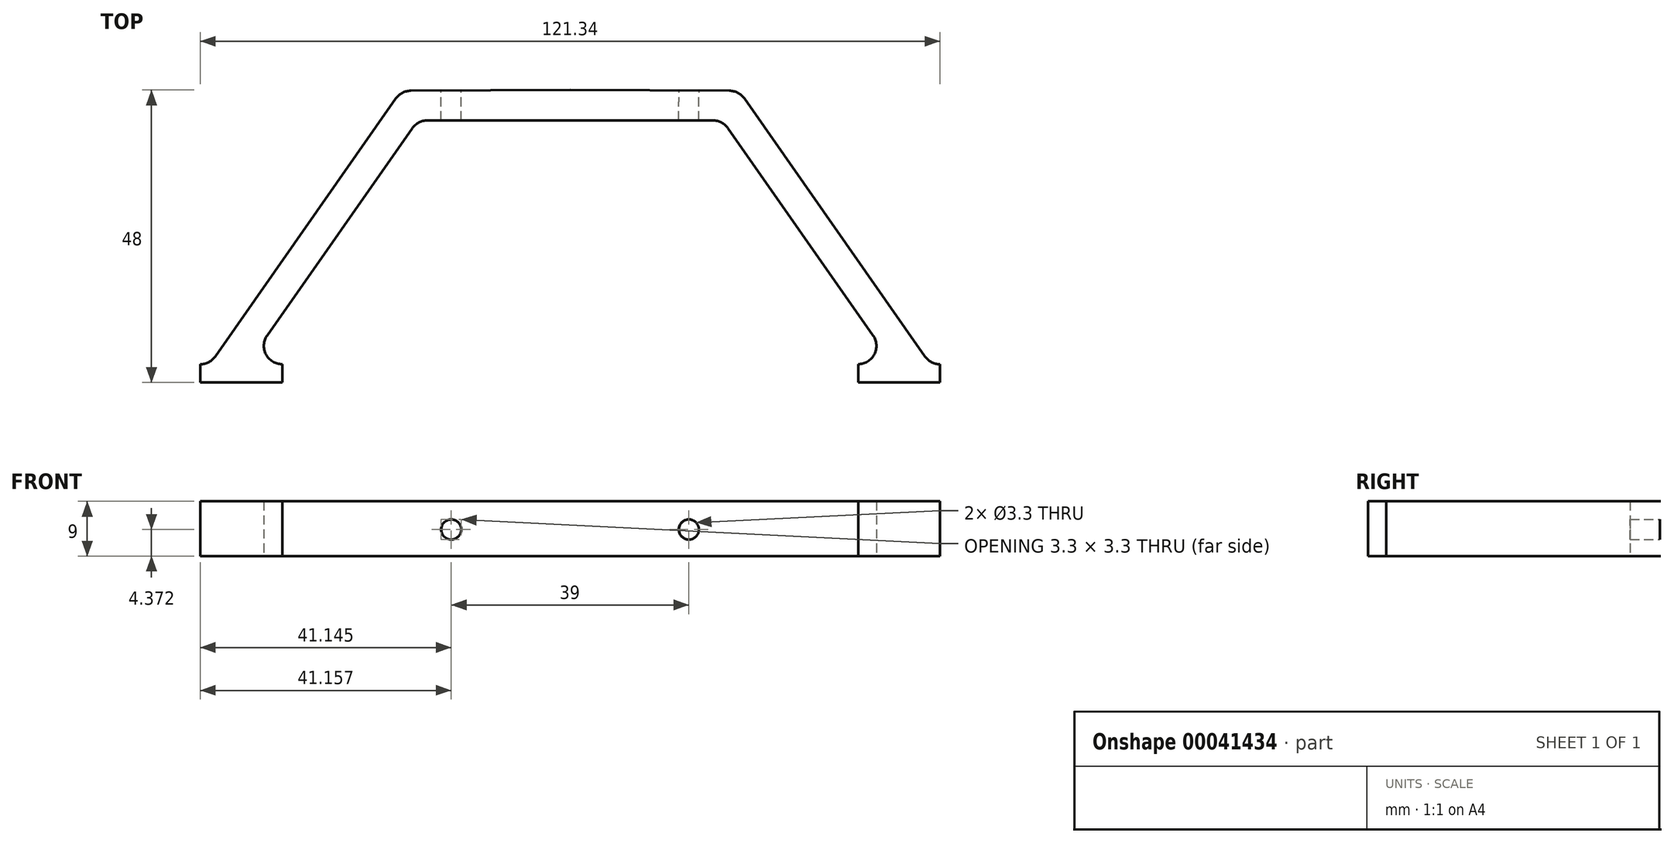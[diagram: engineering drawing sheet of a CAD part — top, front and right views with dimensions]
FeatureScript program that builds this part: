
annotation { "Feature Type Name" : "Feature", "Feature Type Description" : "" }
export const myFeature = defineFeature(function(context is Context, id is Id, definition is map)
    precondition{}
    {
        {
            var Q0;
            Q0=qCreatedBy(makeId("Top.planeOp"),FACE);
            var sketch = newSketch(context, id + "F0", { "sketchPlane" : qUnion([Q0])});
            skLineSegment(sketch, "E0", {"start": v(0, 31.63) * mm, "end": v(0, -36.89) * mm, "construction": true});
            skLineSegment(sketch, "E1", {"start": v(-53.31, 0) * mm, "end": v(57.44, 0) * mm, "construction": true});
            skLineSegment(sketch, "E2.0", {"start": v(-25, 31.63) * mm, "end": v(-25, -36.89) * mm, "construction": true});
            skLineSegment(sketch, "E3", {"start": v(-25.9, -6.28) * mm, "end": v(-49.7, -40.28) * mm});
            skLineSegment(sketch, "E4.0", {"start": v(-28.59, -1.4) * mm, "end": v(-58.22, -43.72) * mm});
            skLineSegment(sketch, "E5.trimOffspring", {"start": v(-23.44, -5) * mm, "end": v(0, -5) * mm});
            skLineSegment(sketch, "E6", {"start": v(0, 0) * mm, "end": v(-26.15, -0.13) * mm});
            skPoint(sketch, "E7.visualSharp", {"position": v(-27.7, -0.14) * mm});
            skArc(sketch, "E7.filletArc", {"start": v(-26.15, -0.13) * mm, "mid": v(-27.52, -0.47) * mm, "end": v(-28.59, -1.4) * mm});
            skPoint(sketch, "E8.visualSharp", {"position": v(-25, -5) * mm});
            skArc(sketch, "E8.filletArc", {"start": v(-23.44, -5) * mm, "mid": v(-24.82, -5.34) * mm, "end": v(-25.9, -6.28) * mm});
            skArc(sketch, "E9.filletArc", {"start": v(-60.67, -45) * mm, "mid": v(-59.29, -44.66) * mm, "end": v(-58.22, -43.72) * mm});
            skArc(sketch, "E10.filletArc", {"start": v(-49.7, -40.28) * mm, "mid": v(-49.9, -43.39) * mm, "end": v(-47.25, -45) * mm});
            skLineSegment(sketch, "E11.top", {"start": v(-60.67, -48) * mm, "end": v(-47.25, -48) * mm});
            skLineSegment(sketch, "E11.left", {"start": v(-60.67, -45) * mm, "end": v(-60.67, -48) * mm});
            skLineSegment(sketch, "E11.right", {"start": v(-47.25, -45) * mm, "end": v(-47.25, -48) * mm});
            skArc(sketch, "E12.MirrorCS", {"start": v(26.15, -0.13) * mm, "mid": v(27.52, -0.47) * mm, "end": v(28.59, -1.4) * mm});
            skArc(sketch, "E13.MirrorCS", {"start": v(23.44, -5) * mm, "mid": v(24.82, -5.34) * mm, "end": v(25.9, -6.28) * mm});
            skLineSegment(sketch, "E14.MirrorCS", {"start": v(47.25, -45) * mm, "end": v(47.25, -48) * mm});
            skPoint(sketch, "E15.MirrorP", {"position": v(25, -5) * mm});
            skLineSegment(sketch, "E16.MirrorCS", {"start": v(25.9, -6.28) * mm, "end": v(49.7, -40.28) * mm});
            skLineSegment(sketch, "E17.MirrorCS", {"start": v(28.59, -1.4) * mm, "end": v(58.22, -43.72) * mm});
            skArc(sketch, "E18.MirrorCS", {"start": v(49.7, -40.28) * mm, "mid": v(49.9, -43.39) * mm, "end": v(47.25, -45) * mm});
            skArc(sketch, "E19.MirrorCS", {"start": v(60.67, -45) * mm, "mid": v(59.29, -44.66) * mm, "end": v(58.22, -43.72) * mm});
            skLineSegment(sketch, "E20.MirrorCS", {"start": v(23.44, -5) * mm, "end": v(0, -5) * mm});
            skLineSegment(sketch, "E21.MirrorCS", {"start": v(0, 0) * mm, "end": v(26.15, -0.13) * mm});
            skPoint(sketch, "E22.MirrorP", {"position": v(27.7, -0.14) * mm});
            skLineSegment(sketch, "E23.MirrorCS", {"start": v(60.67, -45) * mm, "end": v(60.67, -48) * mm});
            skLineSegment(sketch, "E24.MirrorCS", {"start": v(60.67, -48) * mm, "end": v(47.25, -48) * mm});
            skSolve(sketch);
        }
        {
            var Q0;
            Q0=makeQuery(id+"F0.imprint","IMPRINT",FACE,{"disambiguationData":[TD([[makeQuery(id+"F0.imprint","IMPRINT",EDGE,{"derivedFrom":sQuery(id+"F0.wireOp",EDGE,"E3")}),-1.0]])]});
            extrude(context, id + "F1", {"entities" : qUnion([Q0]), "depth" : 9 * mm});
        }
        {
            var Q0;
            Q0=makeQuery(id+"F1.opExtrude","SWEPT_FACE",FACE,{"disambiguationData":[OSD([sQuery(id+"F0.wireOp",EDGE,"E21.MirrorCS")])]});
            var sketch = newSketch(context, id + "F2", { "sketchPlane" : qUnion([Q0])});
            skLineSegment(sketch, "E25", {"start": v(0, -6.97) * mm, "end": v(0, 15.71) * mm, "construction": true});
            skLineSegment(sketch, "E26.0", {"start": v(-19.5, -6.97) * mm, "end": v(-19.5, 15.71) * mm, "construction": true});
            skLineSegment(sketch, "E27", {"start": v(-26.15, 0) * mm, "end": v(26.24, 0) * mm});
            skLineSegment(sketch, "E28.0", {"start": v(-26.15, 4.5) * mm, "end": v(26.24, 4.5) * mm, "construction": true});
            skCircle(sketch, "E29", {"center": v(-19.5, 4.37) * mm, "radius": 1.65 * mm});
            skCircle(sketch, "E30.MirrorC", {"center": v(19.5, 4.37) * mm, "radius": 1.65 * mm});
            skSolve(sketch);
        }
        {
            var Q0;
            Q0 = qSketchRegion(id + "F2", true);
            extrude(context, id + "F3", {"entities" : qUnion([Q0]), "operationType" : NewBodyOperationType.REMOVE, "oppositeDirection" : true, "depth" : 25 * mm});
        }
    });
